# Revit family: 127V BRILLOSA 2835 IP 67_SL127V15W.U_W.W_W.N
name_source: partatom
category: Luminarias
units: mm (PartAtom-declared; Revit-internal decimal feet)

## family parameters
Compartido = No
Corte con vacíos al cargar = No
Cota de conector redondo = Diámetro de uso
Origen de luz = Sí
Punto de cálculo de habitación = No
Se basa en plano de trabajo = Sí
Siempre vertical = No
Tipo de pieza = Normal

## types (3) — shared parameters
Cambio de temperatura de color de luz atenuada = <Ninguno>
Comentarios de vataje = 127V
Fabricante = BRILLANT
Filtro de color = 16777215
Longitud de línea de emisión = 600 mm  [stored 1.9685 ft]
Longitud de símbolo de origen de luz = 1500 mm  [stored 4.92126 ft]
Lámpara = 2835 SMD
Ángulo de campo de foco = 90.00°
Ángulo de enfoque = 30.00°
Ángulo de inclinación = 60.00°
zero-valued in all types: Costo, Elevación por defecto

## per-type parameters (varying)
| type | Descripción | Modelo |
| 127V BRILLOSA 2835 IP 67_SL127V15W.U | TIRA LED BRILLOSA DE PCB CON RECUBRIMIENTO DE PLASTICO 8MM MONOCROMATICA , CON UNA POTENCIA DE 12W/M DE UN TIPO DE LED 2835 SMD, USO PARA INTERIORES COMO EXTERIORES IP67, IRC80, 80 LEDS POR METRO, PRESENTACION DE 50 Y 25M, TEMPERATURA EN BLANCO ULTRA CALIDO 2400K, 1100 LUMENES POR METRO, CORTE A 10CM, ALIMENTADA A 127V, REQUIERE ACCESORIOS COMO CONVERTIDOR DE CORRIENTE (1 POR SEGMENTO DE TIRA), CONECTOR INTERMEDIO (CONSIDERAR EN CORTES DE TIRA O ANGULOS CERRADOS), CONECTOR AGUJA (CONSIDERAR 1PZA POR CADA CONVERTIDOR), FUNDA TERMOCONTRACTIL (CONSIDERAR 2PZAS POR SEGMENTO DE TIRA), TAPA FINAL (CONSIDERAR 1PZA POR SEGMENTO DE TIRA) Y CLIPS DE SUJECION (CONSIDERAR 4 PZAS POR 1M) | SL127V15W.U |
| 127V BRILLOSA 2835 IP 67_SL127V15W.W | TIRA LED BRILLOSA DE PCB CON RECUBRIMIENTO DE PLASTICO 8MM MONOCROMATICA , CON UNA POTENCIA DE 12W/M DE UN TIPO DE LED 2835 SMD, USO PARA INTERIORES COMO EXTERIORES IP67, IRC80, 80 LEDS POR METRO, PRESENTACION DE 50 Y 25M, TEMPERATURA EN BLANCO CALIDO 3000K, 1100 LUMENES POR METRO, CORTE A 10CM, ALIMENTADA A 127V, REQUIERE ACCESORIOS COMO CONVERTIDOR DE CORRIENTE (1 POR SEGMENTO DE TIRA), CONECTOR INTERMEDIO (CONSIDERAR EN CORTES DE TIRA O ANGULOS CERRADOS), CONECTOR AGUJA (CONSIDERAR 1PZA POR CADA CONVERTIDOR), FUNDA TERMOCONTRACTIL (CONSIDERAR 2PZAS POR SEGMENTO DE TIRA), TAPA FINAL (CONSIDERAR 1PZA POR SEGMENTO DE TIRA) Y CLIPS DE SUJECION (CONSIDERAR 4 PZAS POR 1M) | SL127V15W.W |
| 127V BRILLOSA 2835 IP 67_SL127V15W.N | TIRA LED BRILLOSA DE PCB CON RECUBRIMIENTO DE PLASTICO 8MM MONOCROMATICA , CON UNA POTENCIA DE 12W/M DE UN TIPO DE LED 2835 SMD, USO PARA INTERIORES COMO EXTERIORES IP67, IRC80, 80 LEDS POR METRO, PRESENTACION DE 50 Y 25M, TEMPERATURA EN BLANCO FRIO 4000K, 1100 LUMENES POR METRO, CORTE A 10CM, ALIMENTADA A 127V, REQUIERE ACCESORIOS COMO CONVERTIDOR DE CORRIENTE (1 POR SEGMENTO DE TIRA), CONECTOR INTERMEDIO (CONSIDERAR EN CORTES DE TIRA O ANGULOS CERRADOS), CONECTOR AGUJA (CONSIDERAR 1PZA POR CADA CONVERTIDOR), FUNDA TERMOCONTRACTIL (CONSIDERAR 2PZAS POR SEGMENTO DE TIRA), TAPA FINAL (CONSIDERAR 1PZA POR SEGMENTO DE TIRA) Y CLIPS DE SUJECION (CONSIDERAR 4 PZAS POR 1M) | SL127V15W.N |

note: [stored X ft] marks values corroborated as IEEE doubles in the binary element streams (Revit-internal decimal feet)

## geometry (parser evidence)
native form markers: Blend x2
no freeform markers — native parametric forms only
